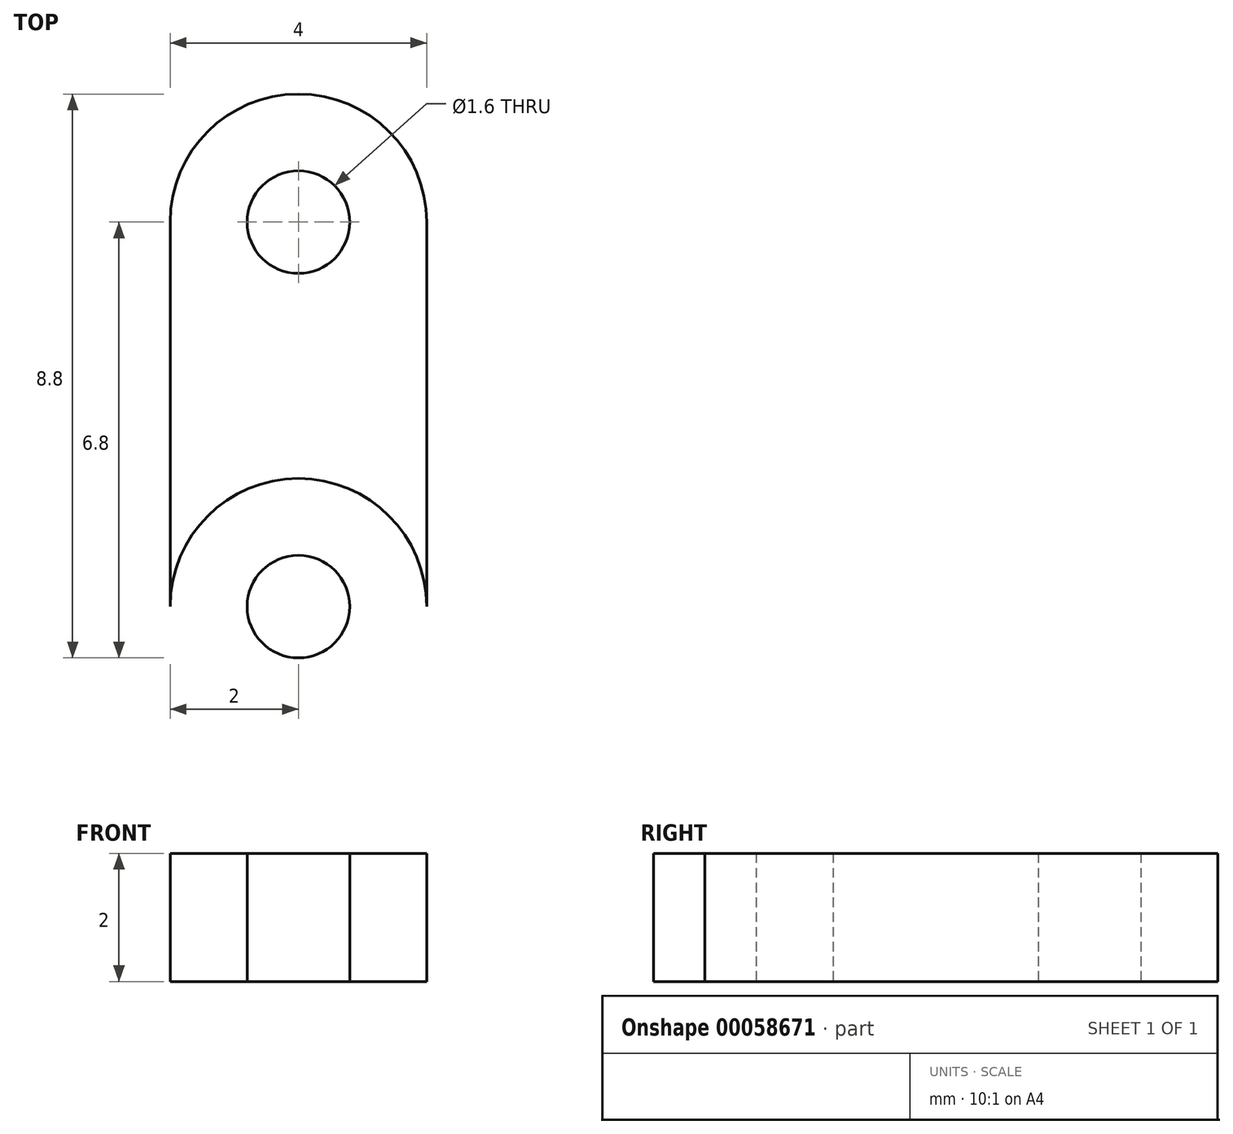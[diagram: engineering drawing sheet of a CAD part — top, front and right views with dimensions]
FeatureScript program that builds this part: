
annotation { "Feature Type Name" : "Feature", "Feature Type Description" : "" }
export const myFeature = defineFeature(function(context is Context, id is Id, definition is map)
    precondition{}
    {
        {
            var Q0;
            Q0=qCreatedBy(makeId("Top.planeOp"),FACE);
            var sketch = newSketch(context, id + "F0", { "sketchPlane" : qUnion([Q0])});
            skLineSegment(sketch, "E0.rect.bottom", {"start": v(-2, 5) * mm, "end": v(2, 5) * mm});
            skLineSegment(sketch, "E0.rect.top", {"start": v(-2, -5) * mm, "end": v(2, -5) * mm});
            skLineSegment(sketch, "E0.rect.left", {"start": v(-2, 5) * mm, "end": v(-2, -5) * mm});
            skLineSegment(sketch, "E0.rect.right", {"start": v(2, 5) * mm, "end": v(2, -5) * mm});
            skPoint(sketch, "E0.rect.middle", {"position": v(0, 0) * mm});
            skCircle(sketch, "E1", {"center": v(0, 3) * mm, "radius": 2 * mm});
            skCircle(sketch, "E2.MirrorC", {"center": v(0, -3) * mm, "radius": 2 * mm});
            skCircle(sketch, "E3", {"center": v(0, 3) * mm, "radius": 0.8 * mm});
            skCircle(sketch, "E4.MirrorC", {"center": v(0, -3) * mm, "radius": 0.8 * mm});
            skSolve(sketch);
        }
        {
            var Q0;
            Q0=makeQuery(id+"F0.imprint","IMPRINT",FACE,{"disambiguationData":[TD([[makeQuery(id+"F0.imprint","IMPRINT",EDGE,{"derivedFrom":sQuery(id+"F0.wireOp",EDGE,"E3")}),-1.0]])]});
            var Q1;
            {var subQ0=sQuery(id+"F0.wireOp",EDGE,"E1");var subQ1=sQuery(id+"F0.wireOp",EDGE,"E0.rect.left");var subQ2=makeQuery(id+"F0.imprint","INTERSECT",VERTEX,{"derivedFrom":[subQ1,subQ0]});Q1=makeQuery(id+"F0.imprint","IMPRINT",FACE,{"disambiguationData":[TD([[makeQuery(id+"F0.imprint","IMPRINT",EDGE,{"disambiguationData":[TD([[subQ2,-1.0]])],"derivedFrom":subQ1}),1.0]])]});}
            var Q2;
            Q2=makeQuery(id+"F0.imprint","IMPRINT",FACE,{"disambiguationData":[TD([[makeQuery(id+"F0.imprint","IMPRINT",EDGE,{"derivedFrom":sQuery(id+"F0.wireOp",EDGE,"E4.MirrorC")}),1.0]])]});
            extrude(context, id + "F1", {"entities" : qUnion([Q0, Q1, Q2]), "depth" : 2 * mm});
        }
    });
